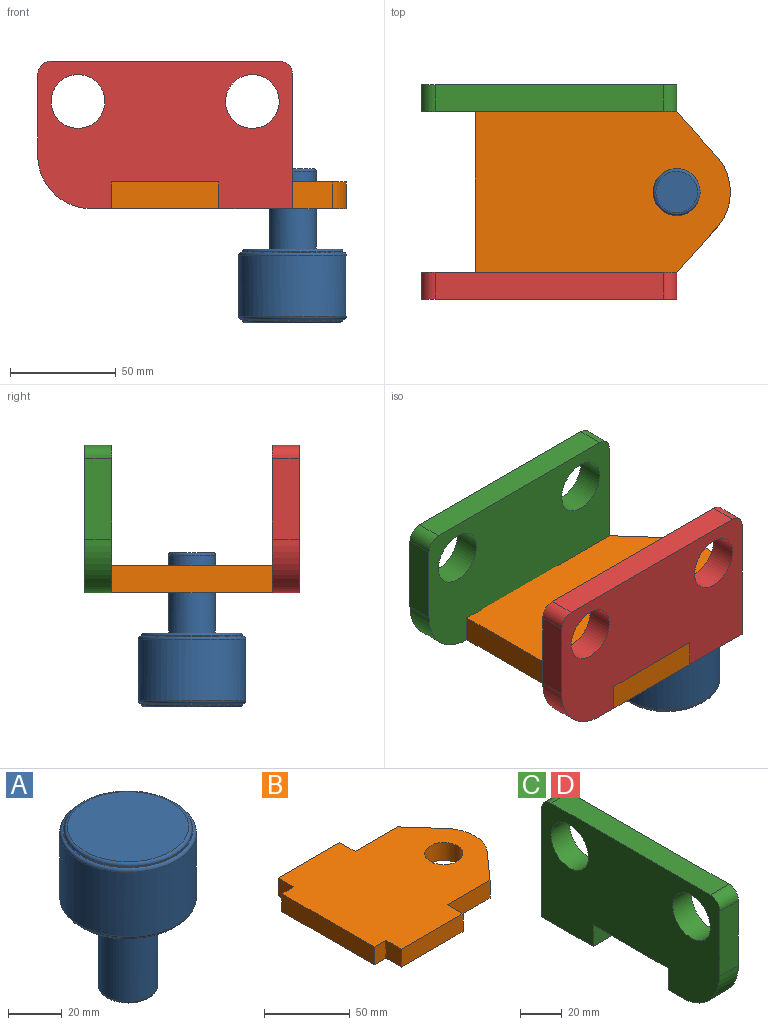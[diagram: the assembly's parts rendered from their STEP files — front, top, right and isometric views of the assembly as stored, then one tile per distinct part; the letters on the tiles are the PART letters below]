
ASSEMBLY  parts=4 mates=3
PART A: 14 faces, bbox 55x55x73 mm
  f0: plane 45.09x45.09mm, normal (0,0,1), area 1596.4mm2, adj f12
  f1: plane 19.69x19.69mm, normal (0,0,-1), area 304.3mm2, adj f13
  f2: cylinder r=11.11mm len=36.83mm, axis (0,0,-1), area 2571.5mm2, adj f3,f13
  f3: plane 45.09x45.09mm, normal (0,0,-1), area 1208.5mm2, adj f2,f9
  f4: cylinder r=23.81mm len=47.63mm, axis (0,0,-1), area 47.5mm2, adj f5,f9
  f5: plane 48.26x48.26mm, normal (0,0,-1), area 47.8mm2, adj f4,f10
  f6: cylinder r=25.4mm len=50.8mm, axis (0,0,-1), area 4661.7mm2, adj f10,f11
  f7: plane 48.26x48.26mm, normal (0,0,1), area 47.8mm2, adj f8,f11
  f8: cylinder r=23.81mm len=47.63mm, axis (0,0,-1), area 47.5mm2, adj f7,f12
  f9: torus R=22.54mm, axis (0,0,1), area 292.7mm2, adj f3,f4
  f10: torus R=24.13mm, axis (0,0,1), area 312.6mm2, adj f5,f6
  f11: torus R=24.13mm, axis (0,0,-1), area 312.6mm2, adj f6,f7
  f12: torus R=22.54mm, axis (0,0,-1), area 292.7mm2, adj f0,f8
  f13: torus R=9.84mm, axis (0,0,1), area 133.5mm2, adj f1,f2
PART B: 17 faces, bbox 120.7x101.6x12.7 mm
  f0: plane 12.7x9.53mm, normal (0,1,0), area 121mm2, adj f1,f13,f15,f16
  f1: plane 76.2x12.7mm, normal (-1,0,0), area 967.7mm2, adj f0,f2,f15,f16
  f2: plane 12.7x9.53mm, normal (0,-1,0), area 121mm2, adj f1,f3,f15,f16
  f3: plane 12.7x12.7mm, normal (-1,0,0), area 161.3mm2, adj f2,f4,f15,f16
  f4: plane 50.8x12.7mm, normal (0,-1,0), area 645.2mm2, adj f3,f5,f15,f16
  f5: plane 12.7x12.7mm, normal (1,0,0), area 161.3mm2, adj f4,f6,f15,f16
  f6: plane 34.93x12.7mm, normal (0,-1,0), area 443.5mm2, adj f5,f7,f15,f16
  f7: plane 21.17x18.93mm, normal (0.75,-0.67,0), area 360.7mm2, adj f6,f8,f15,f16
  f8: cylinder r=25.4mm len=33.87mm, axis (0,0,-1), area 470.8mm2, adj f7,f9,f15,f16
  f9: plane 21.17x18.93mm, normal (0.75,0.67,0), area 360.7mm2, adj f8,f10,f15,f16
  f10: plane 34.93x12.7mm, normal (0,1,0), area 443.5mm2, adj f9,f11,f15,f16
  f11: plane 12.7x12.7mm, normal (1,0,0), area 161.3mm2, adj f10,f12,f15,f16
  f12: plane 50.8x12.7mm, normal (0,1,0), area 645.2mm2, adj f11,f13,f15,f16
  f13: plane 12.7x12.7mm, normal (-1,0,0), area 161.3mm2, adj f0,f12,f15,f16
  f14: cylinder r=11.11mm len=22.23mm, axis (0,0,-1), area 886.7mm2, adj f15,f16
  f15: plane 120.65x101.6mm, normal (0,0,1), area 9352.5mm2, adj f0,f1,f2,f3,f4,f5,f6,f7
  f16: plane 120.65x101.6mm, normal (0,0,-1), area 9352.5mm2, adj f0,f1,f2,f3,f4,f5,f6,f7
PART C: 15 faces, bbox 12.7x120.7x69.9 mm
  f0: plane 38.1x12.7mm, normal (0,-1,0), area 483.9mm2, adj f10,f11,f13,f14
  f1: plane 12.7x9.53mm, normal (0,0,-1), area 121mm2, adj f2,f10,f11,f14
  f2: plane 12.7x12.7mm, normal (0,1,0), area 161.3mm2, adj f1,f3,f10,f11
  f3: plane 50.8x12.7mm, normal (0,0,-1), area 645.2mm2, adj f2,f4,f10,f11
  f4: plane 12.7x12.7mm, normal (0,-1,0), area 161.3mm2, adj f3,f5,f10,f11
  f5: plane 34.93x12.7mm, normal (0,0,-1), area 443.5mm2, adj f4,f6,f10,f11
  f6: plane 63.5x12.7mm, normal (0,1,0), area 806.4mm2, adj f5,f10,f11,f12
  f7: cylinder r=12.7mm len=25.4mm, axis (-1,0,0), area 1013.4mm2, adj f10,f11
  f8: plane 107.95x12.7mm, normal (0,0,1), area 1371mm2, adj f10,f11,f12,f13
  f9: cylinder r=12.7mm len=25.4mm, axis (-1,0,0), area 1013.4mm2, adj f10,f11
  f10: plane 120.65x69.85mm, normal (1,0,0), area 6613.1mm2, adj f0,f1,f2,f3,f4,f5,f6,f7
  f11: plane 120.65x69.85mm, normal (-1,0,0), area 6613.1mm2, adj f0,f1,f2,f3,f4,f5,f6,f7
  f12: cylinder r=6.35mm len=12.7mm, axis (1,0,0), area 126.7mm2, adj f6,f8,f10,f11
  f13: cylinder r=6.35mm len=12.7mm, axis (-1,0,0), area 126.7mm2, adj f0,f8,f10,f11
  f14: cylinder r=25.4mm len=25.4mm, axis (1,0,0), area 506.7mm2, adj f0,f1,f10,f11
PART D: same geometry as C
PLACE A rot(axis=(1,0,0),180deg) t=(-3.76,-96.53,-9.04)mm
PLACE B t=(-3.76,-96.53,8.42)mm
PLACE C rot(axis=(0,0,-1),90deg) t=(-64.09,-45.73,8.42)mm
PLACE D rot(axis=(0,0,-1),90deg) t=(-64.09,-134.63,8.42)mm
MATE fastened A.f2 <-> B.f14  axis (0,0,1) through (-3.76,-96.53,-10.63)mm
MATE fastened D.f3 <-> B.f15  axis (0,0,-1) through (-64.09,-140.98,21.12)mm
MATE fastened C.f3 <-> B.f15  axis (0,0,-1) through (-64.09,-52.08,21.12)mm
